# Revit family: Pump_Commercial-Effluent-Zoeller-160_Automatic_Series_Rev_2
name_source: partatom
category: Mechanical Equipment
revit_build: Autodesk Revit 2018 (Build: 20170223_1515(x64)
units: mm (PartAtom-declared; Revit-internal decimal feet)

## family parameters
Always vertical = No
Cut with Voids When Loaded = No
OmniClass Number = 23.60.30.21
OmniClass Title = Pumps
Part Type = Normal
Room Calculation Point = No
Round Connector Dimension = Use Radius
Shared = Yes
Work Plane-Based = Yes

## types (8) — shared parameters
Cooling = Oil Filled
Cord Length = 240"
Cord Type = UL listed, 3-wire neoprene cord and plug (1 Ph)
Default Elevation = 0"
Description = Sump, Effluent, Dewatering. High Head Flow-Mate 160 Series.
Discharge Diameter = 1 1/2"
Discharge Height = 6"
Discharge Radius = 3/4"
Flow @ 5' = 100 GPM
Hardware = Stainless Steel
Height = 19 5/16"
Hertz = 60
Impeller = Cast Iron
Impeller Type = Non-clogging vortex
Installation Type = Floor Mounted
Insulation = Class B
Lead Wires Insulation = Class B
Length = 10 11/32"
Lower Bearing = Ball bearing
Manufacturer = Zoeller
Material = Cast Iron-Zoeller-Powder Coated Epoxy
Max. Operating Temp. = 130.00 °F
Mechanical Seals = Carbon and Ceramic
Motor Protection = Auto Reset thermal Overload.
Motor Shaft = SAE 1117 carbon steel
Motor Type = Submersible
Off Point = 5 1/4"
On Point = 15 3/4"
Operation = Automatic
Phase = 1
Price = Prices may vary. Please consult Manufacturer Representative for most up-to-date price list.
Product Documentation Link = http://cdn.qleapahead.com
Product Page URL = http://www.zoellerpumps.com
RPM = 3450
Shipping Weight = 80 lbs
Solid Handling = 3/4" Spherical Solids
Square Ring & Gasket = Neoprene
Type = Permanent Split Capacitor
Type Comments = Available in single or double seal designs.
URL = http://www.zoellerpumps.com
Upper Bearing = Ball bearing
Warranty Information = 36 Months (Limited)
Waste Connection = Yes
Width = 8 3/4"

## per-type parameters (varying)
| type | Amps | Apparent Load | Maximum Head | Model | Motor | Voltage |
| M161-115V/1Ph/15.0A/0.5HP | 15 A | 1725 VA | 672" | M161 | 1/2 HP | 115 V |
| D161-230V/1Ph/7.5A/0.5HP | 8 A | 1725 VA | 672" | D161 | 1/2 HP | 230 V |
| H161-200V/1Ph/8.8A/0.5HP | 9 A | 1760 VA | 672" | H161 | 1/2 HP | 200 V |
| M163-115V/1Ph/15.0A/0.5HP | 15 A | 1725 VA | 792" | M163 | 1/2 HP | 115 V |
| D163-230V/1Ph/7.5A/0.5HP | 8 A | 1725 VA | 792" | D163 | 1/2 HP | 230 V |
| H163-200V/1Ph/8.5A/0.5HP | 9 A | 1700 VA | 792" | H163 | 1/2 HP | 200 V |
| D165-230V/1Ph/10.2A/1HP | 10 A | 2346 VA | 1038" | D165 | 1 HP | 230 V |
| H165-200V/1Ph/12.6A/1HP | 13 A | 2520 VA | 1038" | H165 | 1 HP | 200 V |

## geometry (parser evidence)
native form markers: Blend x4, Sweep x2
no freeform markers — native parametric forms only
